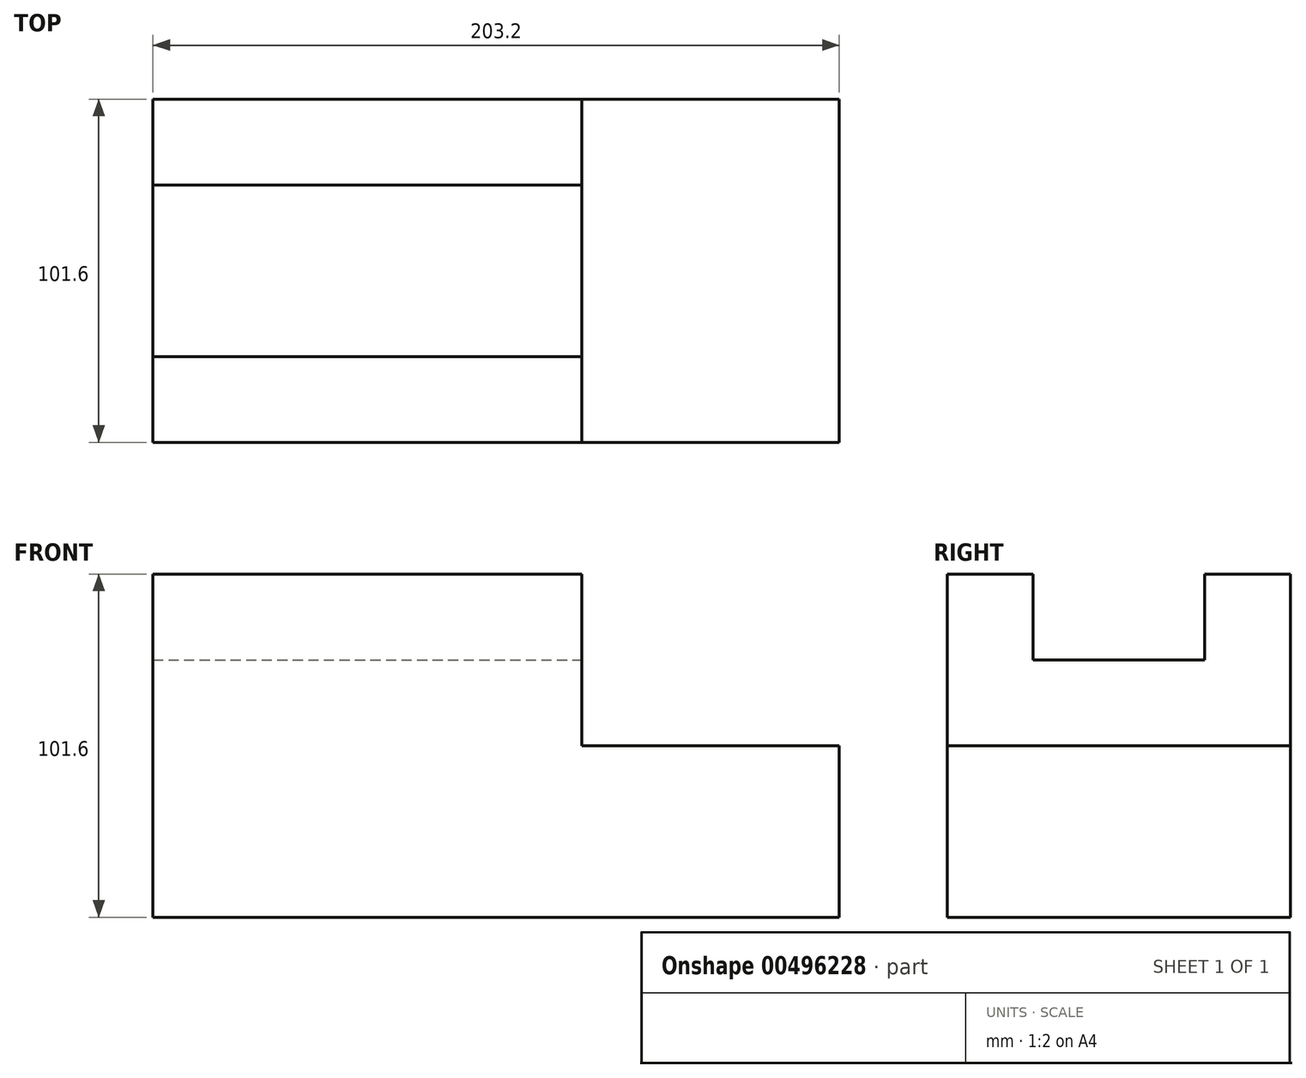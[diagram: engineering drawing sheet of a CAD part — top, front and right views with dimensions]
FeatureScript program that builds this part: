
annotation { "Feature Type Name" : "Feature", "Feature Type Description" : "" }
export const myFeature = defineFeature(function(context is Context, id is Id, definition is map)
    precondition{}
    {
        {
            var Q0;
            Q0=qCreatedBy(makeId("Top.planeOp"),FACE);
            var sketch = newSketch(context, id + "F0", { "sketchPlane" : qUnion([Q0])});
            skLineSegment(sketch, "E0.bottom", {"start": v(-89.13, 0) * mm, "end": v(114.07, 0) * mm});
            skLineSegment(sketch, "E0.top", {"start": v(-89.13, 101.6) * mm, "end": v(114.07, 101.6) * mm});
            skLineSegment(sketch, "E0.left", {"start": v(-89.13, 0) * mm, "end": v(-89.13, 101.6) * mm});
            skLineSegment(sketch, "E0.right", {"start": v(114.07, 0) * mm, "end": v(114.07, 101.6) * mm});
            skSolve(sketch);
        }
        {
            var Q0;
            Q0 = qSketchRegion(id + "F0", true);
            extrude(context, id + "F1", {"entities" : qUnion([Q0]), "depth" : 101.6 * mm});
        }
        {
            var Q0;
            Q0=makeQuery(id+"F1.opExtrude","SWEPT_FACE",FACE,{"disambiguationData":[OSD([sQuery(id+"F0.wireOp",EDGE,"E0.bottom")])]});
            var sketch = newSketch(context, id + "F2", { "sketchPlane" : qUnion([Q0])});
            skLineSegment(sketch, "E1.bottom", {"start": v(114.07, 101.6) * mm, "end": v(37.87, 101.6) * mm});
            skLineSegment(sketch, "E1.top", {"start": v(114.07, 50.8) * mm, "end": v(37.87, 50.8) * mm});
            skLineSegment(sketch, "E1.left", {"start": v(114.07, 101.6) * mm, "end": v(114.07, 50.8) * mm});
            skLineSegment(sketch, "E1.right", {"start": v(37.87, 101.6) * mm, "end": v(37.87, 50.8) * mm});
            skSolve(sketch);
        }
        {
            var Q0;
            Q0 = qSketchRegion(id + "F2", true);
            extrude(context, id + "F3", {"entities" : qUnion([Q0]), "operationType" : NewBodyOperationType.REMOVE, "endBound" : BoundingType.UP_TO_NEXT, "oppositeDirection" : true, "depth" : 25.4 * mm});
        }
        {
            var Q0;
            Q0=makeQuery(id+"F3.boolean.opBoolean","COPY",FACE,{"derivedFrom":makeQuery(id+"F3.opExtrude","SWEPT_FACE",FACE,{"disambiguationData":[OSD([sQuery(id+"F2.wireOp",EDGE,"E1.right")])]})});
            var sketch = newSketch(context, id + "F4", { "sketchPlane" : qUnion([Q0])});
            skLineSegment(sketch, "E2.bottom", {"start": v(25.4, 101.6) * mm, "end": v(76.2, 101.6) * mm});
            skLineSegment(sketch, "E2.top", {"start": v(25.4, 76.2) * mm, "end": v(76.2, 76.2) * mm});
            skLineSegment(sketch, "E2.left", {"start": v(25.4, 101.6) * mm, "end": v(25.4, 76.2) * mm});
            skLineSegment(sketch, "E2.right", {"start": v(76.2, 101.6) * mm, "end": v(76.2, 76.2) * mm});
            skSolve(sketch);
        }
        {
            var Q0;
            Q0 = qSketchRegion(id + "F4", true);
            extrude(context, id + "F5", {"entities" : qUnion([Q0]), "operationType" : NewBodyOperationType.REMOVE, "endBound" : BoundingType.UP_TO_NEXT, "oppositeDirection" : true, "depth" : 25.4 * mm});
        }
    });
